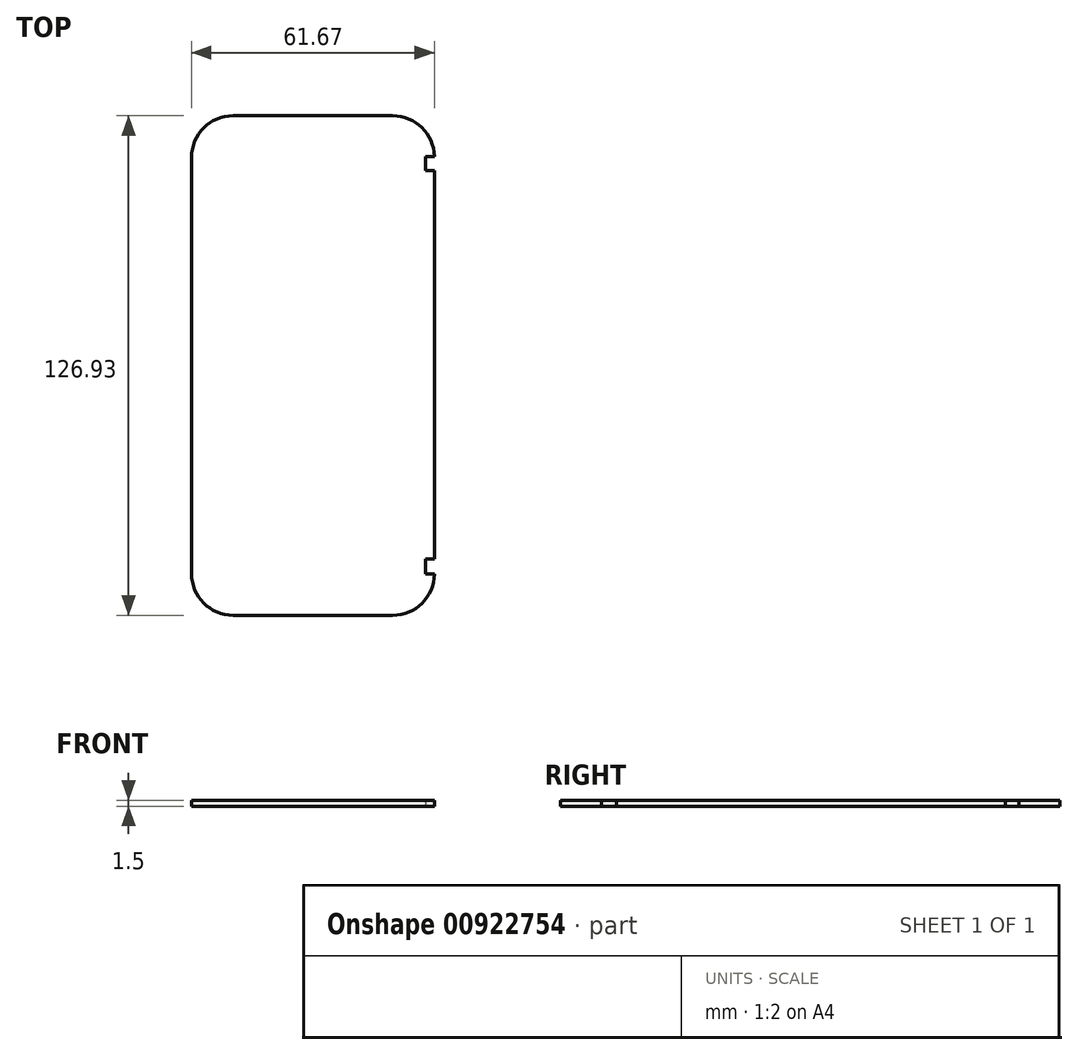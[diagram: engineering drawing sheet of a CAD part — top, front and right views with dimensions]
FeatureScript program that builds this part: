
annotation { "Feature Type Name" : "Feature", "Feature Type Description" : "" }
export const myFeature = defineFeature(function(context is Context, id is Id, definition is map)
    precondition{}
    {
        {
            var Q0;
            Q0=qCreatedBy(makeId("Top.planeOp"),FACE);
            var sketch = newSketch(context, id + "F0", { "sketchPlane" : qUnion([Q0])});
            skLineSegment(sketch, "E0.bottom", {"start": v(-43.9, 51.95) * mm, "end": v(17.77, 51.95) * mm});
            skLineSegment(sketch, "E0.top", {"start": v(-43.9, -74.98) * mm, "end": v(17.77, -74.98) * mm});
            skLineSegment(sketch, "E0.left", {"start": v(-43.9, 51.95) * mm, "end": v(-43.9, -74.98) * mm});
            skLineSegment(sketch, "E0.right", {"start": v(17.77, 51.95) * mm, "end": v(17.77, -74.98) * mm});
            skSolve(sketch);
        }
        {
            var Q0;
            Q0 = qSketchRegion(id + "F0", true);
            extrude(context, id + "F1", {"entities" : qUnion([Q0]), "depth" : 1.5 * mm, "offsetDistance" : 25.4 * mm});
        }
        {
            var Q0;
            Q0=makeQuery(id+"F1.opExtrude","SWEPT_EDGE",EDGE,{"disambiguationData":[OSD([sQuery(id+"F0.wireOp",EDGE,"E0.bottom"),sQuery(id+"F0.wireOp",EDGE,"E0.left")])]});
            var Q1;
            Q1=makeQuery(id+"F1.opExtrude","SWEPT_EDGE",EDGE,{"disambiguationData":[OSD([sQuery(id+"F0.wireOp",EDGE,"E0.bottom"),sQuery(id+"F0.wireOp",EDGE,"E0.right")])]});
            var Q2;
            Q2=makeQuery(id+"F1.opExtrude","SWEPT_EDGE",EDGE,{"disambiguationData":[OSD([sQuery(id+"F0.wireOp",EDGE,"E0.top"),sQuery(id+"F0.wireOp",EDGE,"E0.right")])]});
            var Q3;
            Q3=makeQuery(id+"F1.opExtrude","SWEPT_EDGE",EDGE,{"disambiguationData":[OSD([sQuery(id+"F0.wireOp",EDGE,"E0.top"),sQuery(id+"F0.wireOp",EDGE,"E0.left")])]});
            fillet(context, id + "F2", {"entities" : qUnion([Q0, Q1, Q2, Q3]), "radius" : 10.55 * mm, "tangentPropagation" : true, "allowEdgeOverflow" : false});
        }
        {
            var Q0;
            Q0=makeQuery(id+"F1.opExtrude","CAP_FACE",FACE,{"disambiguationData":[OSD([sQuery(id+"F0.wireOp",EDGE,"E0.bottom"),sQuery(id+"F0.wireOp",EDGE,"E0.top"),sQuery(id+"F0.wireOp",EDGE,"E0.left"),sQuery(id+"F0.wireOp",EDGE,"E0.right")])],"isStart":true});
            var sketch = newSketch(context, id + "F3", { "sketchPlane" : qUnion([Q0])});
            skLineSegment(sketch, "E1.bottom", {"start": v(17.77, 64.54) * mm, "end": v(15.49, 64.54) * mm});
            skLineSegment(sketch, "E1.top", {"start": v(17.77, 60.73) * mm, "end": v(15.49, 60.73) * mm});
            skLineSegment(sketch, "E1.left", {"start": v(17.77, 64.54) * mm, "end": v(17.77, 60.73) * mm});
            skLineSegment(sketch, "E1.right", {"start": v(15.49, 64.54) * mm, "end": v(15.49, 60.73) * mm});
            skLineSegment(sketch, "E2.bottom", {"start": v(17.77, -38.07) * mm, "end": v(15.49, -38.07) * mm});
            skLineSegment(sketch, "E2.top", {"start": v(17.77, -41.6) * mm, "end": v(15.49, -41.6) * mm});
            skLineSegment(sketch, "E2.left", {"start": v(17.77, -38.07) * mm, "end": v(17.77, -41.6) * mm});
            skLineSegment(sketch, "E2.right", {"start": v(15.49, -38.07) * mm, "end": v(15.49, -41.6) * mm});
            skSolve(sketch);
        }
        {
            var Q0;
            Q0 = qSketchRegion(id + "F3", true);
            extrude(context, id + "F4", {"entities" : qUnion([Q0]), "operationType" : NewBodyOperationType.REMOVE, "oppositeDirection" : true, "depth" : 25.4 * mm, "offsetDistance" : 25.4 * mm});
        }
    });
